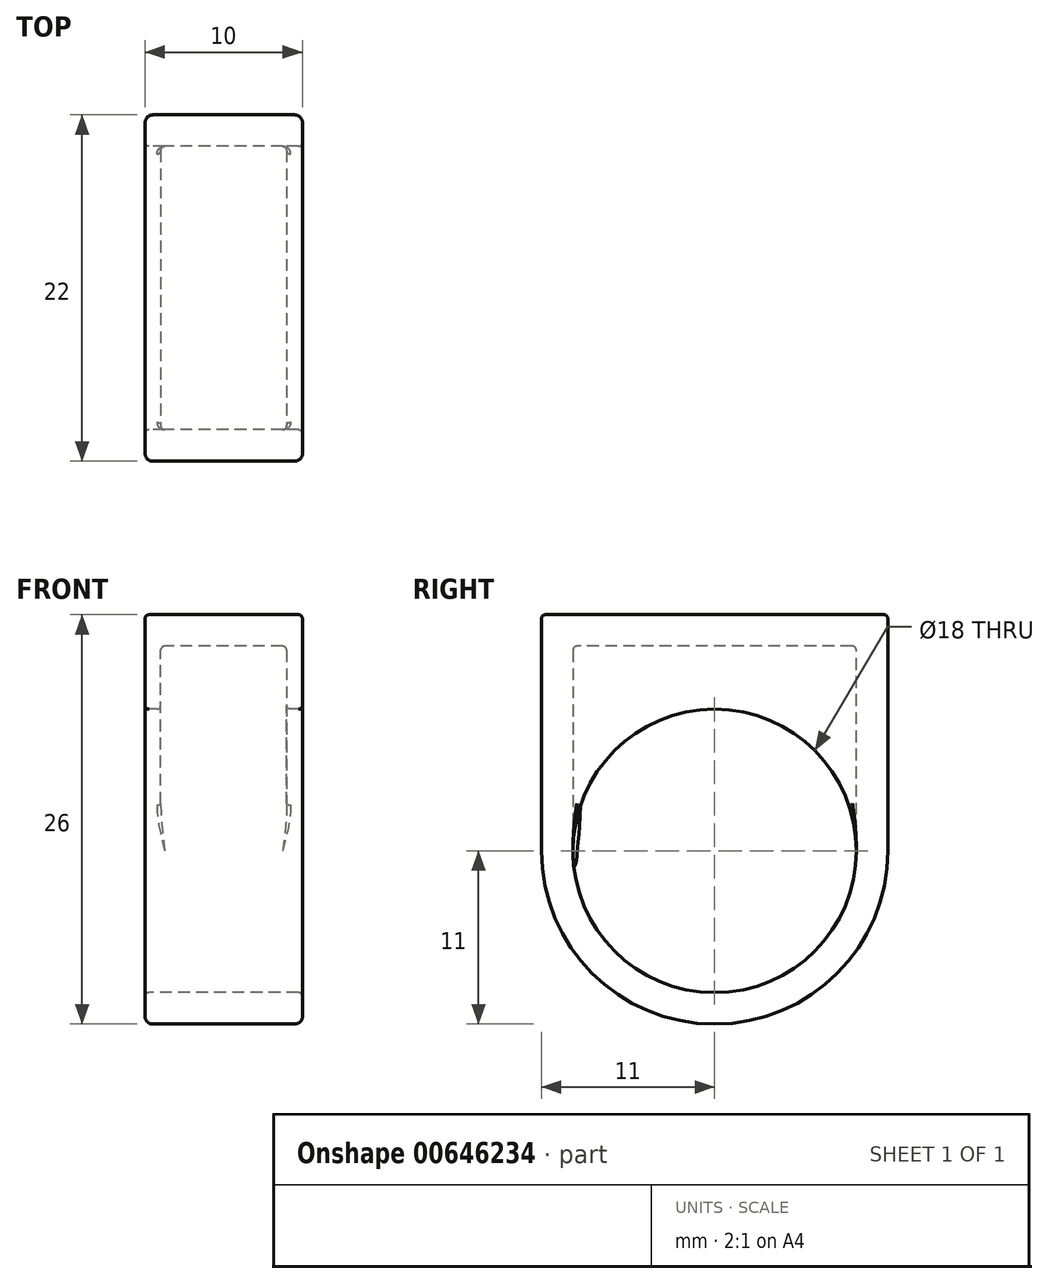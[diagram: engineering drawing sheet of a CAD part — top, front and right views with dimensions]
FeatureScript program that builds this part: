
annotation { "Feature Type Name" : "Feature", "Feature Type Description" : "" }
export const myFeature = defineFeature(function(context is Context, id is Id, definition is map)
    precondition{}
    {
        {
            var Q0;
            Q0=qCreatedBy(makeId("Right.planeOp"),FACE);
            var sketch = newSketch(context, id + "F0", { "sketchPlane" : qUnion([Q0])});
            skCircle(sketch, "E0", {"center": v(0, 0) * mm, "radius": 9 * mm});
            skArc(sketch, "E1", {"start": v(-11, 0) * mm, "mid": v(0, -11) * mm, "end": v(11, 0) * mm});
            skLineSegment(sketch, "E2", {"start": v(-11, 0) * mm, "end": v(-11, 15) * mm});
            skLineSegment(sketch, "E3", {"start": v(11, 0) * mm, "end": v(11, 15) * mm});
            skLineSegment(sketch, "E4", {"start": v(-11, 15) * mm, "end": v(11, 15) * mm});
            skSolve(sketch);
        }
        {
            var Q0;
            Q0 = qSketchRegion(id + "F0", true);
            extrude(context, id + "F1", {"entities" : qUnion([Q0]), "endBound" : BoundingType.SYMMETRIC, "depth" : 10 * mm, "offsetDistance" : 25.4 * mm});
        }
        {
            var Q0;
            Q0=makeQuery(id+"F1.opExtrude","CAP_FACE",FACE,{"disambiguationData":[OSD([sQuery(id+"F0.wireOp",EDGE,"E0"),sQuery(id+"F0.wireOp",EDGE,"E1"),sQuery(id+"F0.wireOp",EDGE,"E2"),sQuery(id+"F0.wireOp",EDGE,"E3"),sQuery(id+"F0.wireOp",EDGE,"E4")])],"isStart":false});
            var sketch = newSketch(context, id + "F2", { "sketchPlane" : qUnion([Q0])});
            skSolve(sketch);
        }
        {
            var Q0;
            Q0=qCreatedBy(makeId("Right.planeOp"),FACE);
            var sketch = newSketch(context, id + "F3", { "sketchPlane" : qUnion([Q0])});
            skLineSegment(sketch, "E5.0", {"start": v(9, 13) * mm, "end": v(-9, 13) * mm});
            skLineSegment(sketch, "E5.1", {"start": v(9, 0) * mm, "end": v(9, 13) * mm});
            skArc(sketch, "E5.2", {"start": v(-9, 0) * mm, "mid": v(0, -9) * mm, "end": v(9, 0) * mm});
            skLineSegment(sketch, "E5.3", {"start": v(-9, 13) * mm, "end": v(-9, 0) * mm});
            skSolve(sketch);
        }
        {
            var Q0;
            Q0 = qSketchRegion(id + "F3", true);
            extrude(context, id + "F4", {"entities" : qUnion([Q0]), "operationType" : NewBodyOperationType.REMOVE, "endBound" : BoundingType.SYMMETRIC, "depth" : 8 * mm, "offsetDistance" : 25.4 * mm});
        }
        {
            var Q0;
            Q0=makeQuery(id+"F1.opExtrude","CAP_EDGE",EDGE,{"disambiguationData":[OSD([sQuery(id+"F0.wireOp",EDGE,"E2")])],"isStart":true});
            var Q1;
            Q1=makeQuery(id+"F1.opExtrude","CAP_EDGE",EDGE,{"disambiguationData":[OSD([sQuery(id+"F0.wireOp",EDGE,"E2")])],"isStart":false});
            fillet(context, id + "F5", {"entities" : qUnion([Q0, Q1]), "radius" : .5 * mm, "tangentPropagation" : true, "allowEdgeOverflow" : false});
        }
        {
            var Q0;
            Q0=makeQuery(id+"F1.opExtrude","CAP_EDGE",EDGE,{"disambiguationData":[OSD([sQuery(id+"F0.wireOp",EDGE,"E0")])],"isStart":false});
            var Q1;
            {var subQ0=sQuery(id+"F0.wireOp",EDGE,"E1");Q1=makeQuery(id+"F5.opFillet","BLEND_EDGE",EDGE,{"blendedFrom":[makeQuery(id+"F1.opExtrude","CAP_EDGE",EDGE,{"disambiguationData":[OSD([subQ0])],"isStart":false}),makeQuery(id+"F1.opExtrude","CAP_FACE",FACE,{"disambiguationData":[OSD([sQuery(id+"F0.wireOp",EDGE,"E0"),subQ0,sQuery(id+"F0.wireOp",EDGE,"E2"),sQuery(id+"F0.wireOp",EDGE,"E3"),sQuery(id+"F0.wireOp",EDGE,"E4")])],"isStart":false})],"blendedInto":[makeQuery(id+"F1.opExtrude","CAP_FACE",FACE,{"disambiguationData":[OSD([sQuery(id+"F0.wireOp",EDGE,"E0"),subQ0,sQuery(id+"F0.wireOp",EDGE,"E2"),sQuery(id+"F0.wireOp",EDGE,"E3"),sQuery(id+"F0.wireOp",EDGE,"E4")])],"isStart":false})]});}
            var Q2;
            Q2=makeQuery(id+"F4.boolean.opBoolean","COPY",EDGE,{"derivedFrom":makeQuery(id+"F4.opExtrude","SWEPT_EDGE",EDGE,{"disambiguationData":[OSD([sQuery(id+"F3.wireOp",EDGE,"E5.2"),sQuery(id+"F3.wireOp",EDGE,"E5.3")])]})});
            var Q3;
            {var subQ0=sQuery(id+"F0.wireOp",EDGE,"E3");Q3=makeQuery(id+"F5.opFillet","BLEND_EDGE",EDGE,{"blendedFrom":[makeQuery(id+"F1.opExtrude","CAP_EDGE",EDGE,{"disambiguationData":[OSD([subQ0])],"isStart":false}),makeQuery(id+"F1.opExtrude","CAP_FACE",FACE,{"disambiguationData":[OSD([sQuery(id+"F0.wireOp",EDGE,"E0"),sQuery(id+"F0.wireOp",EDGE,"E1"),sQuery(id+"F0.wireOp",EDGE,"E2"),subQ0,sQuery(id+"F0.wireOp",EDGE,"E4")])],"isStart":false})],"blendedInto":[makeQuery(id+"F1.opExtrude","CAP_FACE",FACE,{"disambiguationData":[OSD([sQuery(id+"F0.wireOp",EDGE,"E0"),sQuery(id+"F0.wireOp",EDGE,"E1"),sQuery(id+"F0.wireOp",EDGE,"E2"),subQ0,sQuery(id+"F0.wireOp",EDGE,"E4")])],"isStart":false})]});}
            var Q4;
            {var subQ0=sQuery(id+"F0.wireOp",EDGE,"E3");Q4=makeQuery(id+"F5.opFillet","BLEND_EDGE",EDGE,{"blendedFrom":[makeQuery(id+"F1.opExtrude","CAP_EDGE",EDGE,{"disambiguationData":[OSD([subQ0])],"isStart":false}),makeQuery(id+"F1.opExtrude","SWEPT_FACE",FACE,{"disambiguationData":[OSD([subQ0])]})],"blendedInto":[makeQuery(id+"F1.opExtrude","SWEPT_FACE",FACE,{"disambiguationData":[OSD([subQ0])]})]});}
            var Q5;
            Q5=makeQuery(id+"F1.opExtrude","CAP_EDGE",EDGE,{"disambiguationData":[OSD([sQuery(id+"F0.wireOp",EDGE,"E4")])],"isStart":true});
            var Q6;
            Q6=makeQuery(id+"F1.opExtrude","CAP_EDGE",EDGE,{"disambiguationData":[OSD([sQuery(id+"F0.wireOp",EDGE,"E0")])],"isStart":true});
            var Q7;
            Q7=makeQuery(id+"F1.opExtrude","CAP_EDGE",EDGE,{"disambiguationData":[OSD([sQuery(id+"F0.wireOp",EDGE,"E4")])],"isStart":false});
            var Q8;
            {var subQ0=sQuery(id+"F0.wireOp",EDGE,"E3");Q8=makeQuery(id+"F5.opFillet","BLEND_EDGE",EDGE,{"blendedFrom":[makeQuery(id+"F1.opExtrude","CAP_EDGE",EDGE,{"disambiguationData":[OSD([subQ0])],"isStart":true}),makeQuery(id+"F1.opExtrude","SWEPT_FACE",FACE,{"disambiguationData":[OSD([subQ0])]})],"blendedInto":[makeQuery(id+"F1.opExtrude","SWEPT_FACE",FACE,{"disambiguationData":[OSD([subQ0])]})]});}
            var Q9;
            {var subQ0=sQuery(id+"F0.wireOp",EDGE,"E1");Q9=makeQuery(id+"F5.opFillet","BLEND_EDGE",EDGE,{"blendedFrom":[makeQuery(id+"F1.opExtrude","CAP_EDGE",EDGE,{"disambiguationData":[OSD([subQ0])],"isStart":true}),makeQuery(id+"F1.opExtrude","SWEPT_FACE",FACE,{"disambiguationData":[OSD([subQ0])]})],"blendedInto":[makeQuery(id+"F1.opExtrude","SWEPT_FACE",FACE,{"disambiguationData":[OSD([subQ0])]})]});}
            var Q10;
            Q10=makeQuery(id+"F4.boolean.opBoolean","INTERSECT",EDGE,{"derivedFrom":[makeQuery(id+"F1.opExtrude","SWEPT_FACE",FACE,{"disambiguationData":[OSD([sQuery(id+"F0.wireOp",EDGE,"E0")])]}),makeQuery(id+"F4.opExtrude","CAP_FACE",FACE,{"disambiguationData":[OSD([sQuery(id+"F3.wireOp",EDGE,"E5.0"),sQuery(id+"F3.wireOp",EDGE,"E5.1"),sQuery(id+"F3.wireOp",EDGE,"E5.2"),sQuery(id+"F3.wireOp",EDGE,"E5.3")])],"isStart":true})]});
            var Q11;
            Q11=makeQuery(id+"F4.boolean.opBoolean","INTERSECT",EDGE,{"derivedFrom":[makeQuery(id+"F1.opExtrude","SWEPT_FACE",FACE,{"disambiguationData":[OSD([sQuery(id+"F0.wireOp",EDGE,"E0")])]}),makeQuery(id+"F4.opExtrude","CAP_FACE",FACE,{"disambiguationData":[OSD([sQuery(id+"F3.wireOp",EDGE,"E5.0"),sQuery(id+"F3.wireOp",EDGE,"E5.1"),sQuery(id+"F3.wireOp",EDGE,"E5.2"),sQuery(id+"F3.wireOp",EDGE,"E5.3")])],"isStart":false})]});
            var Q12;
            Q12=makeQuery(id+"F1.opExtrude","SWEPT_EDGE",EDGE,{"disambiguationData":[OSD([sQuery(id+"F0.wireOp",EDGE,"E1"),sQuery(id+"F0.wireOp",EDGE,"E3")])]});
            var Q13;
            Q13=makeQuery(id+"F4.boolean.opBoolean","COPY",EDGE,{"derivedFrom":makeQuery(id+"F4.opExtrude","SWEPT_EDGE",EDGE,{"disambiguationData":[OSD([sQuery(id+"F3.wireOp",EDGE,"E5.1"),sQuery(id+"F3.wireOp",EDGE,"E5.2")])]})});
            var Q14;
            Q14=makeQuery(id+"F4.boolean.opBoolean","COPY",EDGE,{"derivedFrom":makeQuery(id+"F4.opExtrude","CAP_EDGE",EDGE,{"disambiguationData":[OSD([sQuery(id+"F3.wireOp",EDGE,"E5.0")])],"isStart":true})});
            var Q15;
            Q15=makeQuery(id+"F4.boolean.opBoolean","COPY",EDGE,{"derivedFrom":makeQuery(id+"F4.opExtrude","CAP_EDGE",EDGE,{"disambiguationData":[OSD([sQuery(id+"F3.wireOp",EDGE,"E5.1")])],"isStart":false})});
            var Q16;
            Q16=makeQuery(id+"F1.opExtrude","SWEPT_EDGE",EDGE,{"disambiguationData":[OSD([sQuery(id+"F0.wireOp",EDGE,"E2"),sQuery(id+"F0.wireOp",EDGE,"E4")])]});
            var Q17;
            {var subQ0=sQuery(id+"F0.wireOp",EDGE,"E1");Q17=makeQuery(id+"F5.opFillet","BLEND_EDGE",EDGE,{"blendedFrom":[makeQuery(id+"F1.opExtrude","CAP_EDGE",EDGE,{"disambiguationData":[OSD([subQ0])],"isStart":true}),makeQuery(id+"F1.opExtrude","CAP_FACE",FACE,{"disambiguationData":[OSD([sQuery(id+"F0.wireOp",EDGE,"E0"),subQ0,sQuery(id+"F0.wireOp",EDGE,"E2"),sQuery(id+"F0.wireOp",EDGE,"E3"),sQuery(id+"F0.wireOp",EDGE,"E4")])],"isStart":true})],"blendedInto":[makeQuery(id+"F1.opExtrude","CAP_FACE",FACE,{"disambiguationData":[OSD([sQuery(id+"F0.wireOp",EDGE,"E0"),subQ0,sQuery(id+"F0.wireOp",EDGE,"E2"),sQuery(id+"F0.wireOp",EDGE,"E3"),sQuery(id+"F0.wireOp",EDGE,"E4")])],"isStart":true})]});}
            var Q18;
            Q18=makeQuery(id+"F4.boolean.opBoolean","COPY",EDGE,{"derivedFrom":makeQuery(id+"F4.opExtrude","SWEPT_EDGE",EDGE,{"disambiguationData":[OSD([sQuery(id+"F3.wireOp",EDGE,"E5.0"),sQuery(id+"F3.wireOp",EDGE,"E5.1")])]})});
            var Q19;
            Q19=makeQuery(id+"F4.boolean.opBoolean","COPY",EDGE,{"derivedFrom":makeQuery(id+"F4.opExtrude","CAP_EDGE",EDGE,{"disambiguationData":[OSD([sQuery(id+"F3.wireOp",EDGE,"E5.0")])],"isStart":false})});
            var Q20;
            Q20=makeQuery(id+"F4.boolean.opBoolean","COPY",EDGE,{"derivedFrom":makeQuery(id+"F4.opExtrude","CAP_EDGE",EDGE,{"disambiguationData":[OSD([sQuery(id+"F3.wireOp",EDGE,"E5.3")])],"isStart":false})});
            var Q21;
            Q21=makeQuery(id+"F5.opFillet","BLEND_EDGE",EDGE,{"blendedFrom":[makeQuery(id+"F1.opExtrude","CAP_EDGE",EDGE,{"disambiguationData":[OSD([sQuery(id+"F0.wireOp",EDGE,"E2")])],"isStart":true}),makeQuery(id+"F1.opExtrude","SWEPT_FACE",FACE,{"disambiguationData":[OSD([sQuery(id+"F0.wireOp",EDGE,"E4")])]})],"blendedInto":[makeQuery(id+"F1.opExtrude","SWEPT_FACE",FACE,{"disambiguationData":[OSD([sQuery(id+"F0.wireOp",EDGE,"E4")])]})]});
            var Q22;
            Q22=makeQuery(id+"F4.boolean.opBoolean","COPY",EDGE,{"derivedFrom":makeQuery(id+"F4.opExtrude","CAP_EDGE",EDGE,{"disambiguationData":[OSD([sQuery(id+"F3.wireOp",EDGE,"E5.1")])],"isStart":true})});
            var Q23;
            Q23=makeQuery(id+"F5.opFillet","BLEND_EDGE",EDGE,{"blendedFrom":[makeQuery(id+"F1.opExtrude","CAP_EDGE",EDGE,{"disambiguationData":[OSD([sQuery(id+"F0.wireOp",EDGE,"E1")])],"isStart":false}),makeQuery(id+"F1.opExtrude","CAP_EDGE",EDGE,{"disambiguationData":[OSD([sQuery(id+"F0.wireOp",EDGE,"E3")])],"isStart":false})],"blendedInto":[]});
            var Q24;
            {var subQ0=sQuery(id+"F0.wireOp",EDGE,"E1");Q24=makeQuery(id+"F5.opFillet","BLEND_EDGE",EDGE,{"blendedFrom":[makeQuery(id+"F1.opExtrude","CAP_EDGE",EDGE,{"disambiguationData":[OSD([subQ0])],"isStart":false}),makeQuery(id+"F1.opExtrude","SWEPT_FACE",FACE,{"disambiguationData":[OSD([subQ0])]})],"blendedInto":[makeQuery(id+"F1.opExtrude","SWEPT_FACE",FACE,{"disambiguationData":[OSD([subQ0])]})]});}
            var Q25;
            Q25=makeQuery(id+"F5.opFillet","BLEND_EDGE",EDGE,{"blendedFrom":[makeQuery(id+"F1.opExtrude","CAP_EDGE",EDGE,{"disambiguationData":[OSD([sQuery(id+"F0.wireOp",EDGE,"E3")])],"isStart":false}),makeQuery(id+"F1.opExtrude","SWEPT_FACE",FACE,{"disambiguationData":[OSD([sQuery(id+"F0.wireOp",EDGE,"E4")])]})],"blendedInto":[makeQuery(id+"F1.opExtrude","SWEPT_FACE",FACE,{"disambiguationData":[OSD([sQuery(id+"F0.wireOp",EDGE,"E4")])]})]});
            var Q26;
            Q26=makeQuery(id+"F5.opFillet","BLEND_EDGE",EDGE,{"blendedFrom":[makeQuery(id+"F1.opExtrude","CAP_EDGE",EDGE,{"disambiguationData":[OSD([sQuery(id+"F0.wireOp",EDGE,"E1")])],"isStart":true}),makeQuery(id+"F1.opExtrude","CAP_EDGE",EDGE,{"disambiguationData":[OSD([sQuery(id+"F0.wireOp",EDGE,"E3")])],"isStart":true})],"blendedInto":[]});
            var Q27;
            Q27=makeQuery(id+"F4.boolean.opBoolean","COPY",EDGE,{"derivedFrom":makeQuery(id+"F4.opExtrude","CAP_EDGE",EDGE,{"disambiguationData":[OSD([sQuery(id+"F3.wireOp",EDGE,"E5.3")])],"isStart":true})});
            var Q28;
            Q28=makeQuery(id+"F5.opFillet","BLEND_EDGE",EDGE,{"blendedFrom":[makeQuery(id+"F1.opExtrude","CAP_EDGE",EDGE,{"disambiguationData":[OSD([sQuery(id+"F0.wireOp",EDGE,"E2")])],"isStart":false}),makeQuery(id+"F1.opExtrude","SWEPT_FACE",FACE,{"disambiguationData":[OSD([sQuery(id+"F0.wireOp",EDGE,"E4")])]})],"blendedInto":[makeQuery(id+"F1.opExtrude","SWEPT_FACE",FACE,{"disambiguationData":[OSD([sQuery(id+"F0.wireOp",EDGE,"E4")])]})]});
            var Q29;
            Q29=makeQuery(id+"F5.opFillet","BLEND_EDGE",EDGE,{"blendedFrom":[makeQuery(id+"F1.opExtrude","CAP_EDGE",EDGE,{"disambiguationData":[OSD([sQuery(id+"F0.wireOp",EDGE,"E3")])],"isStart":true}),makeQuery(id+"F1.opExtrude","SWEPT_FACE",FACE,{"disambiguationData":[OSD([sQuery(id+"F0.wireOp",EDGE,"E4")])]})],"blendedInto":[makeQuery(id+"F1.opExtrude","SWEPT_FACE",FACE,{"disambiguationData":[OSD([sQuery(id+"F0.wireOp",EDGE,"E4")])]})]});
            var Q30;
            Q30=makeQuery(id+"F1.opExtrude","SWEPT_EDGE",EDGE,{"disambiguationData":[OSD([sQuery(id+"F0.wireOp",EDGE,"E1"),sQuery(id+"F0.wireOp",EDGE,"E2")])]});
            var Q31;
            Q31=makeQuery(id+"F5.opFillet","BLEND_EDGE",EDGE,{"blendedFrom":[makeQuery(id+"F1.opExtrude","CAP_EDGE",EDGE,{"disambiguationData":[OSD([sQuery(id+"F0.wireOp",EDGE,"E1")])],"isStart":false}),makeQuery(id+"F1.opExtrude","CAP_EDGE",EDGE,{"disambiguationData":[OSD([sQuery(id+"F0.wireOp",EDGE,"E2")])],"isStart":false})],"blendedInto":[]});
            var Q32;
            {var subQ0=sQuery(id+"F0.wireOp",EDGE,"E2");Q32=makeQuery(id+"F5.opFillet","BLEND_EDGE",EDGE,{"blendedFrom":[makeQuery(id+"F1.opExtrude","CAP_EDGE",EDGE,{"disambiguationData":[OSD([subQ0])],"isStart":true}),makeQuery(id+"F1.opExtrude","SWEPT_FACE",FACE,{"disambiguationData":[OSD([subQ0])]})],"blendedInto":[makeQuery(id+"F1.opExtrude","SWEPT_FACE",FACE,{"disambiguationData":[OSD([subQ0])]})]});}
            var Q33;
            Q33=makeQuery(id+"F1.opExtrude","SWEPT_EDGE",EDGE,{"disambiguationData":[OSD([sQuery(id+"F0.wireOp",EDGE,"E3"),sQuery(id+"F0.wireOp",EDGE,"E4")])]});
            var Q34;
            Q34=makeQuery(id+"F4.boolean.opBoolean","COPY",EDGE,{"derivedFrom":makeQuery(id+"F4.opExtrude","SWEPT_EDGE",EDGE,{"disambiguationData":[OSD([sQuery(id+"F3.wireOp",EDGE,"E5.0"),sQuery(id+"F3.wireOp",EDGE,"E5.3")])]})});
            var Q35;
            {var subQ0=sQuery(id+"F0.wireOp",EDGE,"E2");Q35=makeQuery(id+"F5.opFillet","BLEND_EDGE",EDGE,{"blendedFrom":[makeQuery(id+"F1.opExtrude","CAP_EDGE",EDGE,{"disambiguationData":[OSD([subQ0])],"isStart":false}),makeQuery(id+"F1.opExtrude","CAP_FACE",FACE,{"disambiguationData":[OSD([sQuery(id+"F0.wireOp",EDGE,"E0"),sQuery(id+"F0.wireOp",EDGE,"E1"),subQ0,sQuery(id+"F0.wireOp",EDGE,"E3"),sQuery(id+"F0.wireOp",EDGE,"E4")])],"isStart":false})],"blendedInto":[makeQuery(id+"F1.opExtrude","CAP_FACE",FACE,{"disambiguationData":[OSD([sQuery(id+"F0.wireOp",EDGE,"E0"),sQuery(id+"F0.wireOp",EDGE,"E1"),subQ0,sQuery(id+"F0.wireOp",EDGE,"E3"),sQuery(id+"F0.wireOp",EDGE,"E4")])],"isStart":false})]});}
            var Q36;
            {var subQ0=sQuery(id+"F0.wireOp",EDGE,"E3");Q36=makeQuery(id+"F5.opFillet","BLEND_EDGE",EDGE,{"blendedFrom":[makeQuery(id+"F1.opExtrude","CAP_EDGE",EDGE,{"disambiguationData":[OSD([subQ0])],"isStart":true}),makeQuery(id+"F1.opExtrude","CAP_FACE",FACE,{"disambiguationData":[OSD([sQuery(id+"F0.wireOp",EDGE,"E0"),sQuery(id+"F0.wireOp",EDGE,"E1"),sQuery(id+"F0.wireOp",EDGE,"E2"),subQ0,sQuery(id+"F0.wireOp",EDGE,"E4")])],"isStart":true})],"blendedInto":[makeQuery(id+"F1.opExtrude","CAP_FACE",FACE,{"disambiguationData":[OSD([sQuery(id+"F0.wireOp",EDGE,"E0"),sQuery(id+"F0.wireOp",EDGE,"E1"),sQuery(id+"F0.wireOp",EDGE,"E2"),subQ0,sQuery(id+"F0.wireOp",EDGE,"E4")])],"isStart":true})]});}
            var Q37;
            {var subQ0=sQuery(id+"F0.wireOp",EDGE,"E2");Q37=makeQuery(id+"F5.opFillet","BLEND_EDGE",EDGE,{"blendedFrom":[makeQuery(id+"F1.opExtrude","CAP_EDGE",EDGE,{"disambiguationData":[OSD([subQ0])],"isStart":true}),makeQuery(id+"F1.opExtrude","CAP_FACE",FACE,{"disambiguationData":[OSD([sQuery(id+"F0.wireOp",EDGE,"E0"),sQuery(id+"F0.wireOp",EDGE,"E1"),subQ0,sQuery(id+"F0.wireOp",EDGE,"E3"),sQuery(id+"F0.wireOp",EDGE,"E4")])],"isStart":true})],"blendedInto":[makeQuery(id+"F1.opExtrude","CAP_FACE",FACE,{"disambiguationData":[OSD([sQuery(id+"F0.wireOp",EDGE,"E0"),sQuery(id+"F0.wireOp",EDGE,"E1"),subQ0,sQuery(id+"F0.wireOp",EDGE,"E3"),sQuery(id+"F0.wireOp",EDGE,"E4")])],"isStart":true})]});}
            var Q38;
            {var subQ0=sQuery(id+"F0.wireOp",EDGE,"E2");Q38=makeQuery(id+"F5.opFillet","BLEND_EDGE",EDGE,{"blendedFrom":[makeQuery(id+"F1.opExtrude","CAP_EDGE",EDGE,{"disambiguationData":[OSD([subQ0])],"isStart":false}),makeQuery(id+"F1.opExtrude","SWEPT_FACE",FACE,{"disambiguationData":[OSD([subQ0])]})],"blendedInto":[makeQuery(id+"F1.opExtrude","SWEPT_FACE",FACE,{"disambiguationData":[OSD([subQ0])]})]});}
            var Q39;
            Q39=makeQuery(id+"F5.opFillet","BLEND_EDGE",EDGE,{"blendedFrom":[makeQuery(id+"F1.opExtrude","CAP_EDGE",EDGE,{"disambiguationData":[OSD([sQuery(id+"F0.wireOp",EDGE,"E1")])],"isStart":true}),makeQuery(id+"F1.opExtrude","CAP_EDGE",EDGE,{"disambiguationData":[OSD([sQuery(id+"F0.wireOp",EDGE,"E2")])],"isStart":true})],"blendedInto":[]});
            fillet(context, id + "F6", {"entities" : qUnion([Q0, Q1, Q2, Q3, Q4, Q5, Q6, Q7, Q8, Q9, Q10, Q11, Q12, Q13, Q14, Q15, Q16, Q17, Q18, Q19, Q20, Q21, Q22, Q23, Q24, Q25, Q26, Q27, Q28, Q29, Q30, Q31, Q32, Q33, Q34, Q35, Q36, Q37, Q38, Q39]), "radius" : .25 * mm, "tangentPropagation" : true, "allowEdgeOverflow" : false});
        }
    });
